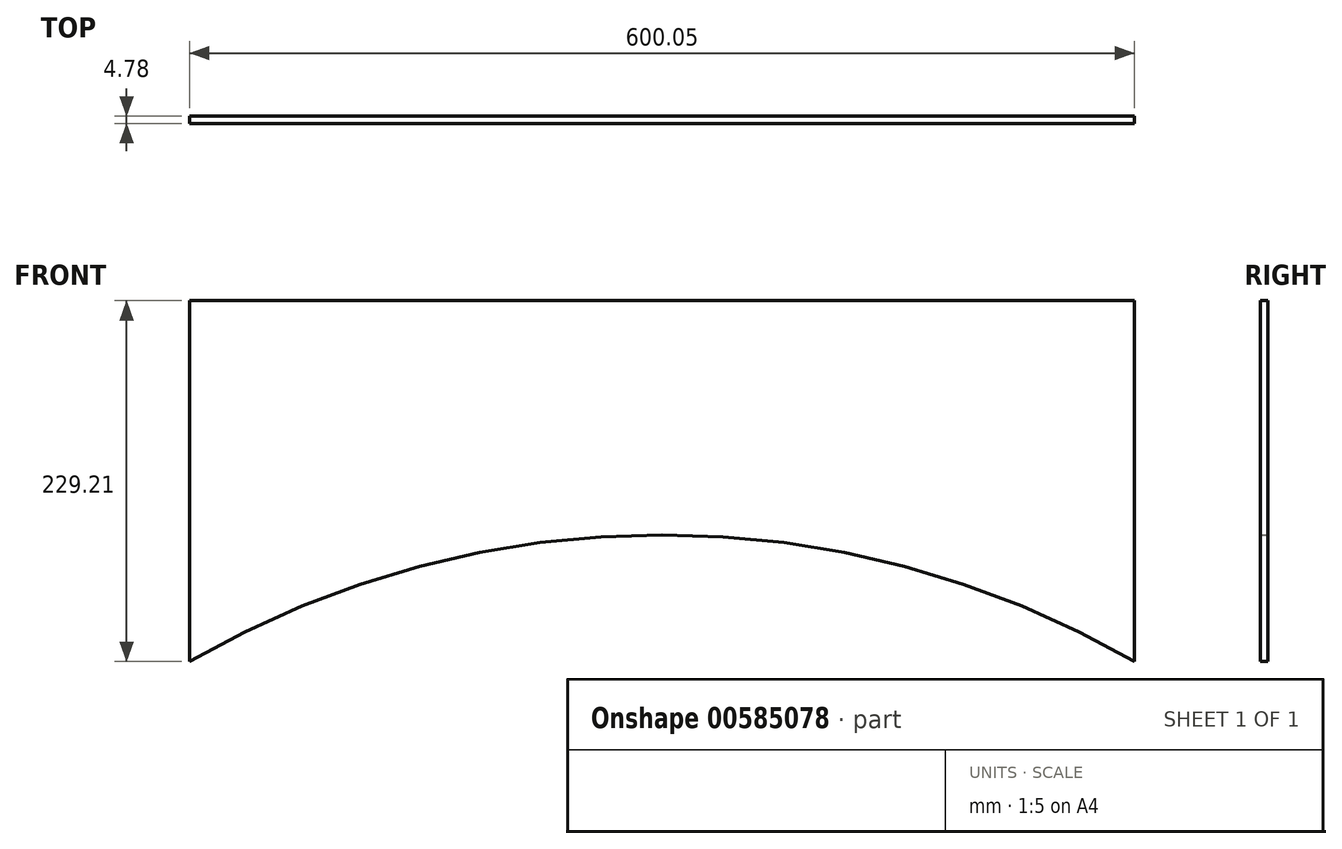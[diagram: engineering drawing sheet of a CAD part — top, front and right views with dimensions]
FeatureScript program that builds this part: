
annotation { "Feature Type Name" : "Feature", "Feature Type Description" : "" }
export const myFeature = defineFeature(function(context is Context, id is Id, definition is map)
    precondition{}
    {
        {
            var Q0;
            Q0=qCreatedBy(makeId("Front.planeOp"),FACE);
            var sketch = newSketch(context, id + "F0", { "sketchPlane" : qUnion([Q0])});
            skLineSegment(sketch, "E0.top", {"start": v(0, 229.2) * mm, "end": v(600.05, 229.2) * mm});
            skLineSegment(sketch, "E0.left", {"start": v(0, 0) * mm, "end": v(0, 229.2) * mm});
            skArc(sketch, "E1", {"start": v(600.05, 0) * mm, "mid": v(300.02, 80.51) * mm, "end": v(0, 0) * mm});
            skLineSegment(sketch, "E2", {"start": v(600.05, 229.2) * mm, "end": v(600.05, 0) * mm});
            skSolve(sketch);
        }
        {
            var Q0;
            Q0=makeQuery(id+"F0.imprint","IMPRINT",FACE,{"disambiguationData":[TD([[makeQuery(id+"F0.imprint","IMPRINT",EDGE,{"derivedFrom":sQuery(id+"F0.wireOp",EDGE,"E0.top")}),-1.0]])]});
            extrude(context, id + "F1", {"entities" : qUnion([Q0]), "depth" : 4.78 * mm, "offsetDistance" : 25.4 * mm});
        }
    });
